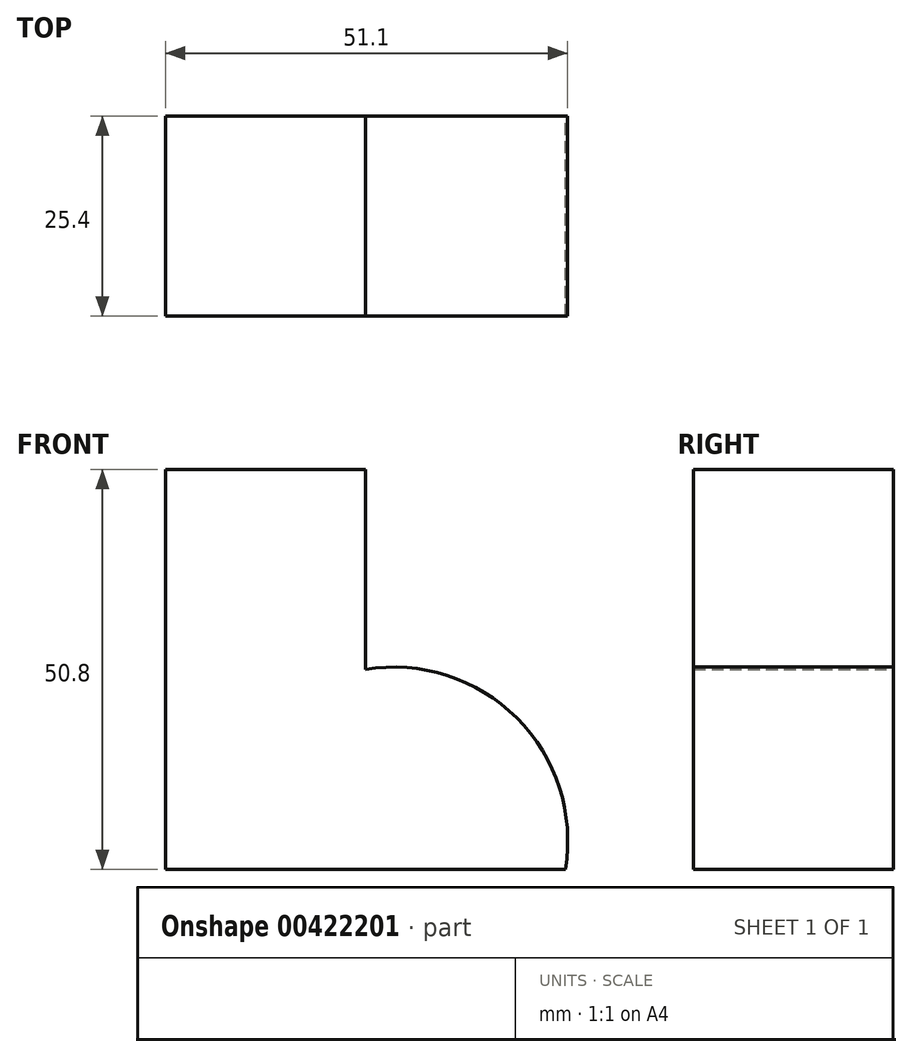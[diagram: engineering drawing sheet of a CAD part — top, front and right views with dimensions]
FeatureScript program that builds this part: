
annotation { "Feature Type Name" : "Feature", "Feature Type Description" : "" }
export const myFeature = defineFeature(function(context is Context, id is Id, definition is map)
    precondition{}
    {
        {
            var Q0;
            Q0=qCreatedBy(makeId("Front.planeOp"),FACE);
            var sketch = newSketch(context, id + "F0", { "sketchPlane" : qUnion([Q0])});
            skLineSegment(sketch, "E0", {"start": v(0, 0) * mm, "end": v(50.8, 0) * mm});
            skLineSegment(sketch, "E1", {"start": v(0, 0) * mm, "end": v(0, 50.8) * mm});
            skLineSegment(sketch, "E2", {"start": v(0, 50.8) * mm, "end": v(25.4, 50.8) * mm});
            skLineSegment(sketch, "E3", {"start": v(25.4, 50.8) * mm, "end": v(25.4, 25.4) * mm});
            skArc(sketch, "E4", {"start": v(50.8, 0) * mm, "mid": v(44.64, 19.24) * mm, "end": v(25.4, 25.4) * mm});
            skSolve(sketch);
        }
        {
            var Q0;
            Q0=makeQuery(id+"F0.imprint","IMPRINT",FACE,{"disambiguationData":[TD([[makeQuery(id+"F0.imprint","IMPRINT",EDGE,{"derivedFrom":sQuery(id+"F0.wireOp",EDGE,"E0")}),1.0]])]});
            extrude(context, id + "F1", {"entities" : qUnion([Q0]), "depth" : 25.4 * mm});
        }
    });
